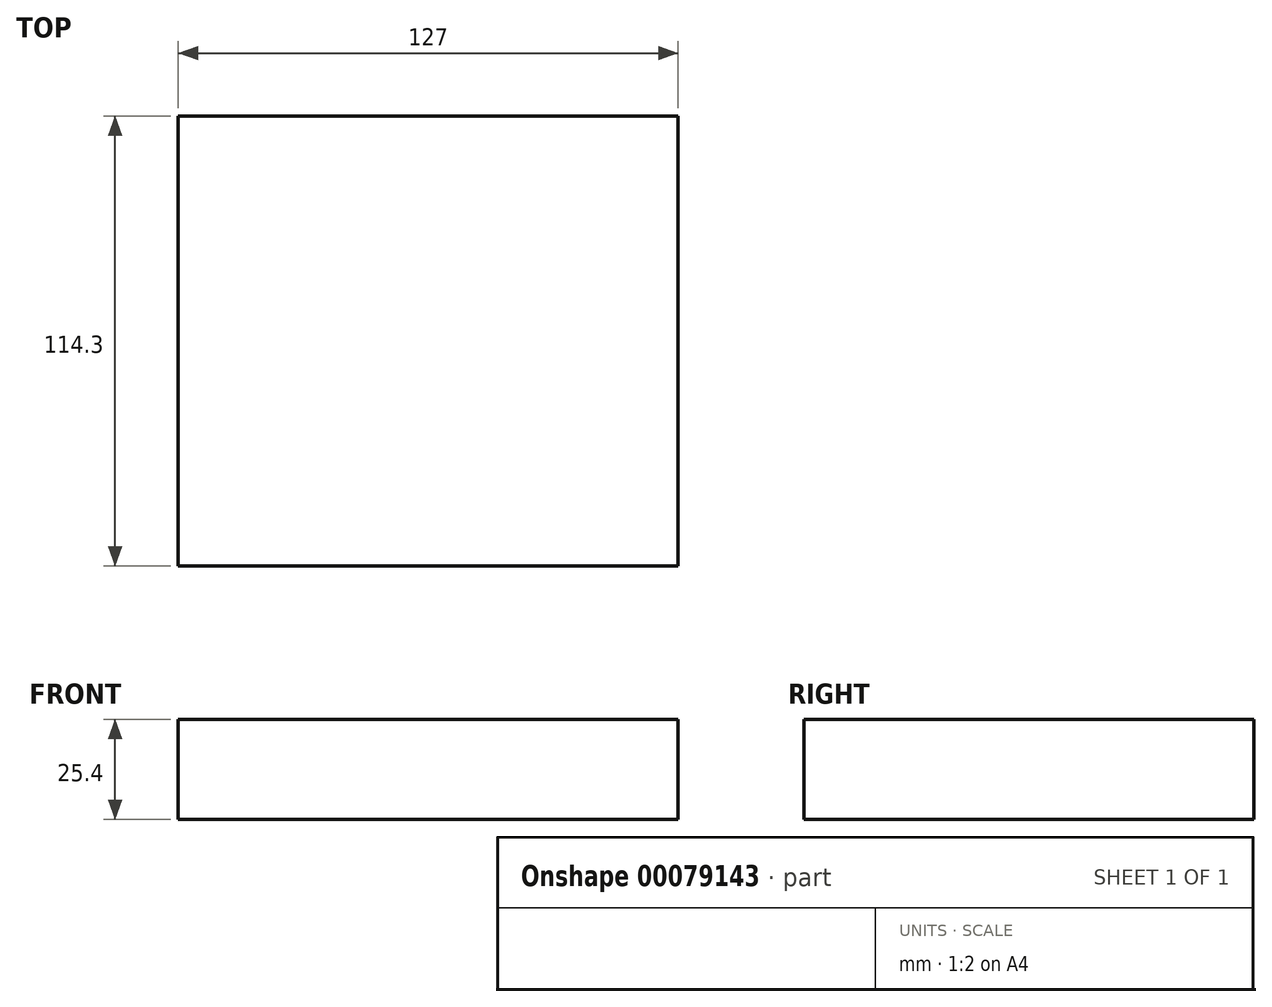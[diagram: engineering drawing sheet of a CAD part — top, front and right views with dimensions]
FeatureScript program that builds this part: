
annotation { "Feature Type Name" : "Feature", "Feature Type Description" : "" }
export const myFeature = defineFeature(function(context is Context, id is Id, definition is map)
    precondition{}
    {
        {
            var Q0;
            Q0=qCreatedBy(makeId("Top.planeOp"),FACE);
            var sketch = newSketch(context, id + "F0", { "sketchPlane" : qUnion([Q0])});
            skLineSegment(sketch, "E0", {"start": v(0, 0) * mm, "end": v(0, 57.15) * mm, "construction": true});
            skLineSegment(sketch, "E1", {"start": v(0, 57.15) * mm, "end": v(-63.5, 57.15) * mm, "construction": true});
            skLineSegment(sketch, "E2", {"start": v(-63.5, 57.15) * mm, "end": v(63.5, 57.15) * mm});
            skLineSegment(sketch, "E3", {"start": v(-63.5, 57.15) * mm, "end": v(-63.5, -57.15) * mm});
            skLineSegment(sketch, "E4", {"start": v(63.5, 57.15) * mm, "end": v(63.5, -57.15) * mm});
            skLineSegment(sketch, "E5", {"start": v(63.5, -57.15) * mm, "end": v(-63.5, -57.15) * mm});
            skSolve(sketch);
        }
        {
            var Q0;
            Q0=makeQuery(id+"F0.imprint","IMPRINT",FACE,{"disambiguationData":[TD([[makeQuery(id+"F0.imprint","IMPRINT",EDGE,{"derivedFrom":sQuery(id+"F0.wireOp",EDGE,"E2")}),-1.0]])]});
            extrude(context, id + "F1", {"entities" : qUnion([Q0]), "depth" : 25.4 * mm});
        }
    });
